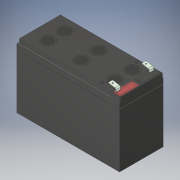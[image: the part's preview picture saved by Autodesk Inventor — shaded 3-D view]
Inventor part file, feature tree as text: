
AUTODESK INVENTOR PART (.ipt)
format: ipt  version: 2018 (Build 220112000, 112)  size: 305,152 bytes
history: native  units: in
note: dims shown in document units (in); Inventor stores cm internally (conversion verified against a paired STEP export)
features: fillet x1
ambient origin geometry x8: Origin, YZ Plane, XZ Plane, XY Plane, X Axis, Y Axis, Z Axis, Center Point
bodies: Solid1 (feature_tree)
feature tree (1):
  fillet  "Congé6"  [1 undecoded]
note: 1 required parameter value undecoded (feature->parameter linkage not recoverable at this tier; creation-order binding heuristic only, values carry confidence <= 0.55)
